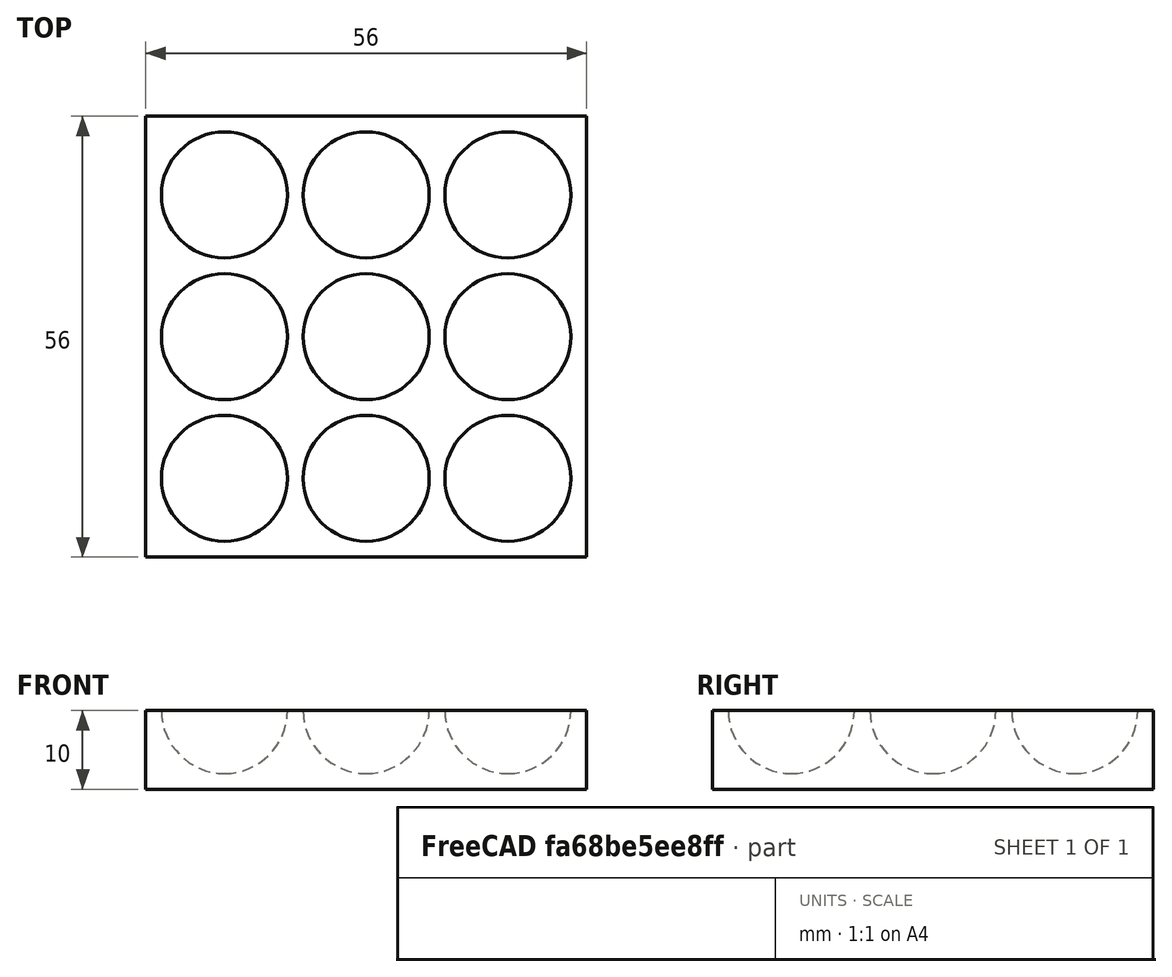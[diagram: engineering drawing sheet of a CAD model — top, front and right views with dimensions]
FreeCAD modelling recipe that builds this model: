
FCSTD DOCUMENT  (FreeCAD 0.18.4R)
Label: tutorial_freecad_ex13_a
License: All rights reserved
LicenseURL: http://en.wikipedia.org/wiki/All_rights_reserved
objects: Part::Sphere×1, Part::FeaturePython×1, Part::Box×1, Part::Cut×1
note: 4 computed .brp shape members not serialized (recipe doc carries the construction recipe); baked Part::Feature solids carry a one-line shape summary decoded from their .brp

FEATURE [Part::Sphere] Sphere  label="Esfera"
  Angle1 = -90
  Angle2 = 90
  Angle3 = 360
  AttacherType = Attacher::AttachEngine3D
  Radius = 8
FEATURE [Part::FeaturePython] Array  # Draft array (typed FeaturePython)
  Angle = 360
  ArrayType = 0
  Axis = (0,0,1)
  Base = -> Sphere
  Center = (0,0,0)
  Fuse = false
  IntervalAxis = (0,0,0)
  IntervalX = (18,0,0)
  IntervalY = (0,18,0)
  IntervalZ = (0,0,1)
  NumberPolar = 1
  NumberX = 3
  NumberY = 3
  NumberZ = 1
  Placement = pos=(10,10,10) rot=(0,0,1;0rad)
FEATURE [Part::Box] Box  label="Cubo"
  AttacherType = Attacher::AttachEngine3D
  Height = 10
  Length = 56
  Width = 56
FEATURE [Part::Cut] Cut
  Base = -> Box
  Refine = true
  Tool = -> Array
